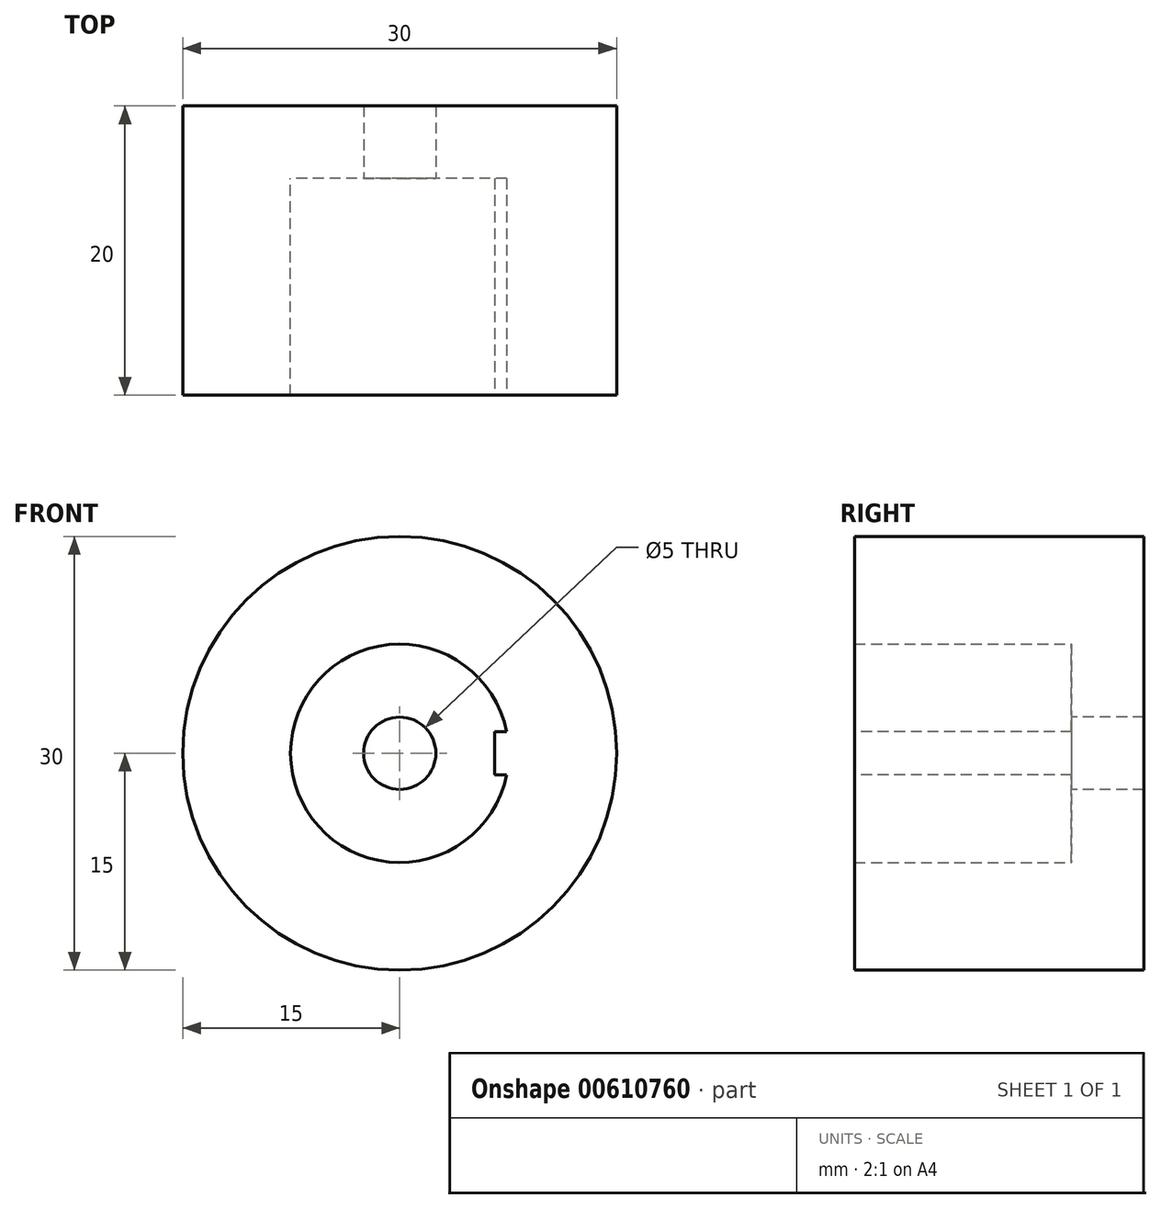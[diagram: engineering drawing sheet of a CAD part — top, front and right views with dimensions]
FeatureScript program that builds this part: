
annotation { "Feature Type Name" : "Feature", "Feature Type Description" : "" }
export const myFeature = defineFeature(function(context is Context, id is Id, definition is map)
    precondition{}
    {
        {
            var Q0;
            Q0=qCreatedBy(makeId("Front.planeOp"),FACE);
            var sketch = newSketch(context, id + "F0", { "sketchPlane" : qUnion([Q0])});
            skCircle(sketch, "E0", {"center": v(0, 0) * mm, "radius": 7.55 * mm});
            skCircle(sketch, "E1", {"center": v(0, 0) * mm, "radius": 15 * mm});
            skSolve(sketch);
        }
        {
            var Q0;
            Q0=makeQuery(id+"F0.imprint","IMPRINT",FACE,{"disambiguationData":[TD([[makeQuery(id+"F0.imprint","IMPRINT",EDGE,{"derivedFrom":sQuery(id+"F0.wireOp",EDGE,"E0")}),-1.0]])]});
            extrude(context, id + "F1", {"entities" : qUnion([Q0]), "depth" : 15 * mm, "offsetDistance" : 25 * mm});
        }
        {
            var Q0;
            Q0=makeQuery(id+"F1.opExtrude","CAP_FACE",FACE,{"disambiguationData":[OSD([sQuery(id+"F0.wireOp",EDGE,"E0"),sQuery(id+"F0.wireOp",EDGE,"E1")])],"isStart":true});
            var sketch = newSketch(context, id + "F2", { "sketchPlane" : qUnion([Q0])});
            skCircle(sketch, "E2", {"center": v(0, 0) * mm, "radius": 15 * mm});
            skCircle(sketch, "E3", {"center": v(0, 0) * mm, "radius": 2.5 * mm});
            skSolve(sketch);
        }
        {
            var Q0;
            Q0 = qSketchRegion(id + "F2", true);
            extrude(context, id + "F3", {"entities" : qUnion([Q0]), "operationType" : NewBodyOperationType.ADD, "depth" : 5 * mm, "offsetDistance" : 25 * mm});
        }
        {
            var Q0;
            Q0=makeQuery(id+"F1.opExtrude","CAP_FACE",FACE,{"disambiguationData":[OSD([sQuery(id+"F0.wireOp",EDGE,"E0"),sQuery(id+"F0.wireOp",EDGE,"E1")])],"isStart":false});
            var sketch = newSketch(context, id + "F4", { "sketchPlane" : qUnion([Q0])});
            skLineSegment(sketch, "E4.bottom", {"start": v(7.4, 1.5) * mm, "end": v(6.55, 1.5) * mm});
            skLineSegment(sketch, "E4.top", {"start": v(7.4, -1.5) * mm, "end": v(6.55, -1.5) * mm});
            skLineSegment(sketch, "E4.right", {"start": v(6.55, 1.5) * mm, "end": v(6.55, -1.5) * mm});
            skArc(sketch, "E5", {"start": v(7.4, -1.5) * mm, "mid": v(7.55, 0) * mm, "end": v(7.4, 1.5) * mm});
            skSolve(sketch);
        }
        {
            var Q0;
            Q0 = qSketchRegion(id + "F4", true);
            extrude(context, id + "F5", {"entities" : qUnion([Q0]), "operationType" : NewBodyOperationType.ADD, "oppositeDirection" : true, "depth" : 15 * mm, "offsetDistance" : 25 * mm});
        }
    });
